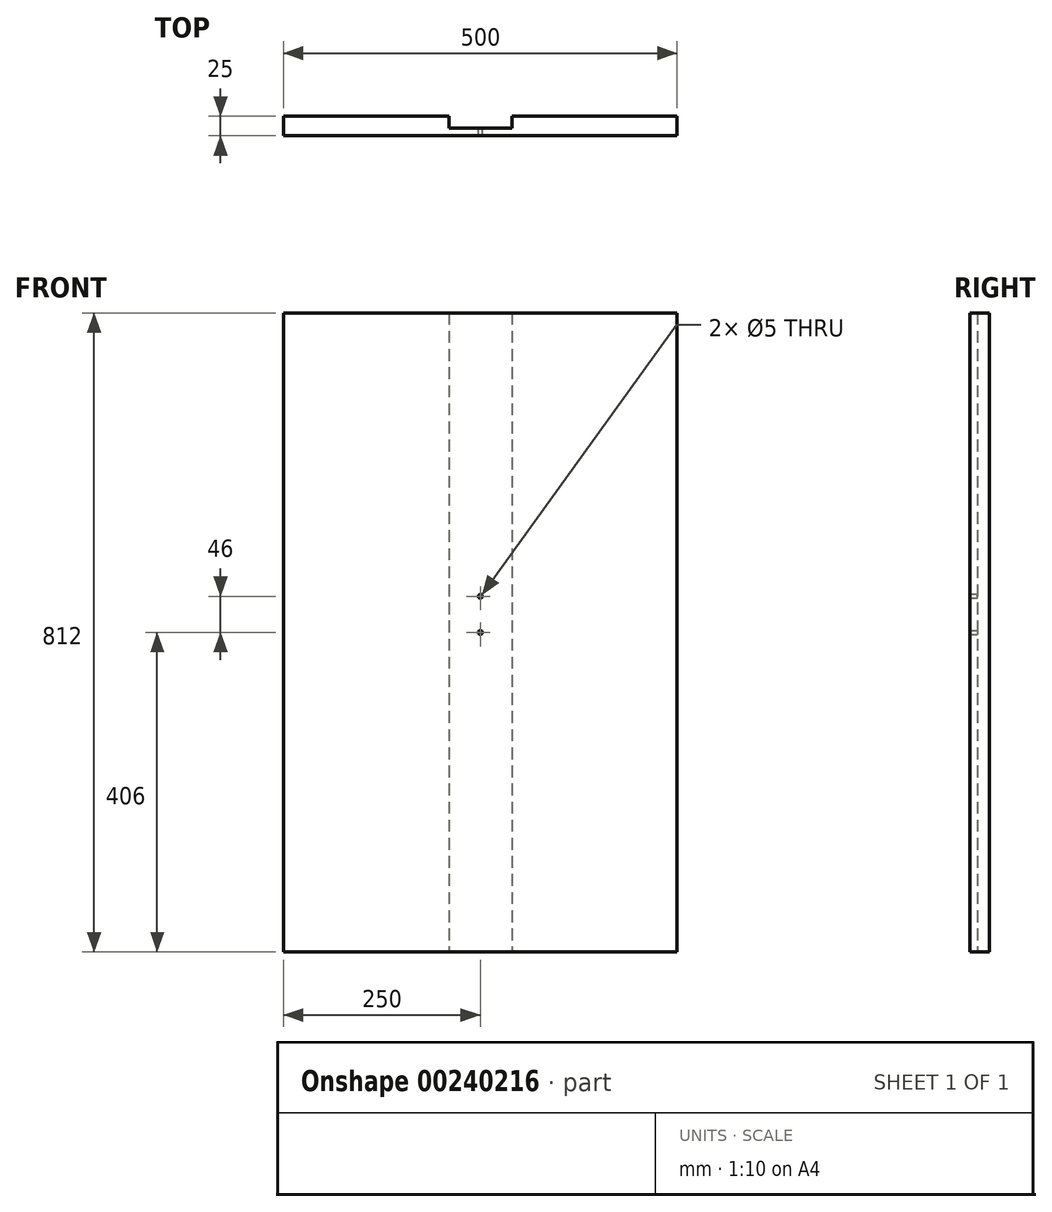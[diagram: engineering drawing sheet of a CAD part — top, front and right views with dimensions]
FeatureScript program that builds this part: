
annotation { "Feature Type Name" : "Feature", "Feature Type Description" : "" }
export const myFeature = defineFeature(function(context is Context, id is Id, definition is map)
    precondition{}
    {
        {
            var Q0;
            Q0=qCreatedBy(makeId("Top.planeOp"),FACE);
            var sketch = newSketch(context, id + "F0", { "sketchPlane" : qUnion([Q0])});
            skLineSegment(sketch, "E0", {"start": v(-238.65, 0) * mm, "end": v(-238.65, -25) * mm});
            skLineSegment(sketch, "E1", {"start": v(-238.65, -25) * mm, "end": v(261.35, -25) * mm});
            skLineSegment(sketch, "E2", {"start": v(261.35, -25) * mm, "end": v(261.35, 0) * mm});
            skLineSegment(sketch, "E3", {"start": v(261.35, 0) * mm, "end": v(51.35, 0) * mm});
            skLineSegment(sketch, "E4", {"start": v(51.35, 0) * mm, "end": v(51.35, -15) * mm});
            skLineSegment(sketch, "E5", {"start": v(51.35, -15) * mm, "end": v(-28.65, -15) * mm});
            skLineSegment(sketch, "E6", {"start": v(-28.65, -15) * mm, "end": v(-28.65, 0) * mm});
            skLineSegment(sketch, "E7", {"start": v(-28.65, 0) * mm, "end": v(-238.65, 0) * mm});
            skSolve(sketch);
        }
        {
            var Q0;
            Q0 = qSketchRegion(id + "F0", true);
            extrude(context, id + "F1", {"entities" : qUnion([Q0]), "depth" : 812 * mm});
        }
        {
            var Q0;
            Q0=makeQuery(id+"F1.opExtrude","SWEPT_FACE",FACE,{"disambiguationData":[OSD([sQuery(id+"F0.wireOp",EDGE,"E5")])]});
            var sketch = newSketch(context, id + "F2", { "sketchPlane" : qUnion([Q0])});
            skLineSegment(sketch, "E8", {"start": v(-51.35, 406) * mm, "end": v(-11.35, 406) * mm, "construction": true});
            skLineSegment(sketch, "E9", {"start": v(-11.35, 406) * mm, "end": v(28.65, 406) * mm, "construction": true});
            skLineSegment(sketch, "E10", {"start": v(-11.35, 406) * mm, "end": v(-11.35, 812) * mm, "construction": true});
            skLineSegment(sketch, "E11", {"start": v(-11.35, 406) * mm, "end": v(-11.35, 0) * mm, "construction": true});
            skCircle(sketch, "E12", {"center": v(-11.35, 406) * mm, "radius": 2.5 * mm});
            skSolve(sketch);
        }
        {
            var Q0;
            Q0 = qSketchRegion(id + "F2", true);
            extrude(context, id + "F3", {"entities" : qUnion([Q0]), "operationType" : NewBodyOperationType.REMOVE, "endBound" : BoundingType.THROUGH_ALL, "oppositeDirection" : true, "depth" : 25 * mm});
        }
        {
            var Q0;
            Q0=makeQuery(id+"F1.opExtrude","SWEPT_FACE",FACE,{"disambiguationData":[OSD([sQuery(id+"F0.wireOp",EDGE,"E1")])]});
            var sketch = newSketch(context, id + "F4", { "sketchPlane" : qUnion([Q0])});
            skLineSegment(sketch, "E13", {"start": v(-238.65, 452) * mm, "end": v(11.35, 452) * mm, "construction": true});
            skLineSegment(sketch, "E14", {"start": v(11.35, 452) * mm, "end": v(261.35, 452) * mm, "construction": true});
            skLineSegment(sketch, "E15", {"start": v(11.35, 452) * mm, "end": v(11.35, 812) * mm, "construction": true});
            skCircle(sketch, "E16", {"center": v(11.35, 452) * mm, "radius": 2.5 * mm});
            skSolve(sketch);
        }
        {
            var Q0;
            Q0 = qSketchRegion(id + "F4", true);
            extrude(context, id + "F5", {"entities" : qUnion([Q0]), "operationType" : NewBodyOperationType.REMOVE, "endBound" : BoundingType.THROUGH_ALL, "oppositeDirection" : true, "depth" : 25 * mm});
        }
    });
